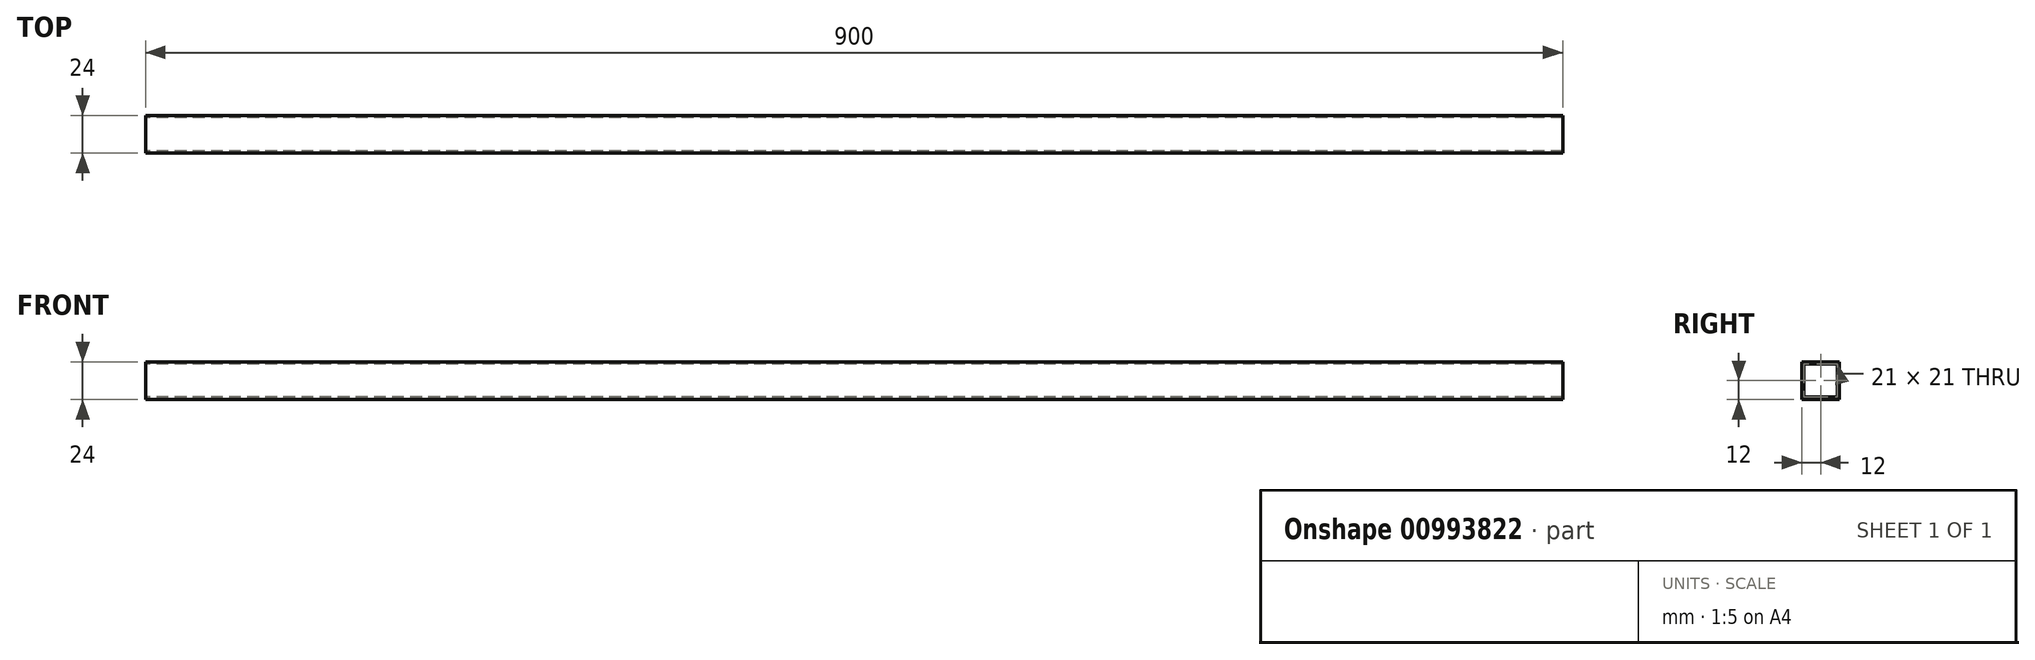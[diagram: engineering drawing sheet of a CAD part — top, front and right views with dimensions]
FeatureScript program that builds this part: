
annotation { "Feature Type Name" : "Feature", "Feature Type Description" : "" }
export const myFeature = defineFeature(function(context is Context, id is Id, definition is map)
    precondition{}
    {
        {
            var Q0;
            Q0=qCreatedBy(makeId("Right.planeOp"),FACE);
            var sketch = newSketch(context, id + "F0", { "sketchPlane" : qUnion([Q0])});
            skLineSegment(sketch, "E0.bottom", {"start": v(12, 12) * mm, "end": v(-12, 12) * mm});
            skLineSegment(sketch, "E0.top", {"start": v(12, -12) * mm, "end": v(-12, -12) * mm});
            skLineSegment(sketch, "E0.left", {"start": v(12, 12) * mm, "end": v(12, -12) * mm});
            skLineSegment(sketch, "E0.right", {"start": v(-12, 12) * mm, "end": v(-12, -12) * mm});
            skPoint(sketch, "E0.middle", {"position": v(0, 0) * mm});
            skLineSegment(sketch, "E1.bottom", {"start": v(10.5, 10.5) * mm, "end": v(-10.5, 10.5) * mm});
            skLineSegment(sketch, "E1.top", {"start": v(10.5, -10.5) * mm, "end": v(-10.5, -10.5) * mm});
            skLineSegment(sketch, "E1.left", {"start": v(10.5, 10.5) * mm, "end": v(10.5, -10.5) * mm});
            skLineSegment(sketch, "E1.right", {"start": v(-10.5, 10.5) * mm, "end": v(-10.5, -10.5) * mm});
            skSolve(sketch);
        }
        {
            var Q0;
            Q0 = qSketchRegion(id + "F0", true);
            extrude(context, id + "F1", {"entities" : qUnion([Q0]), "depth" : 900 * mm, "offsetDistance" : 25 * mm, "symmetric" : true});
        }
    });
